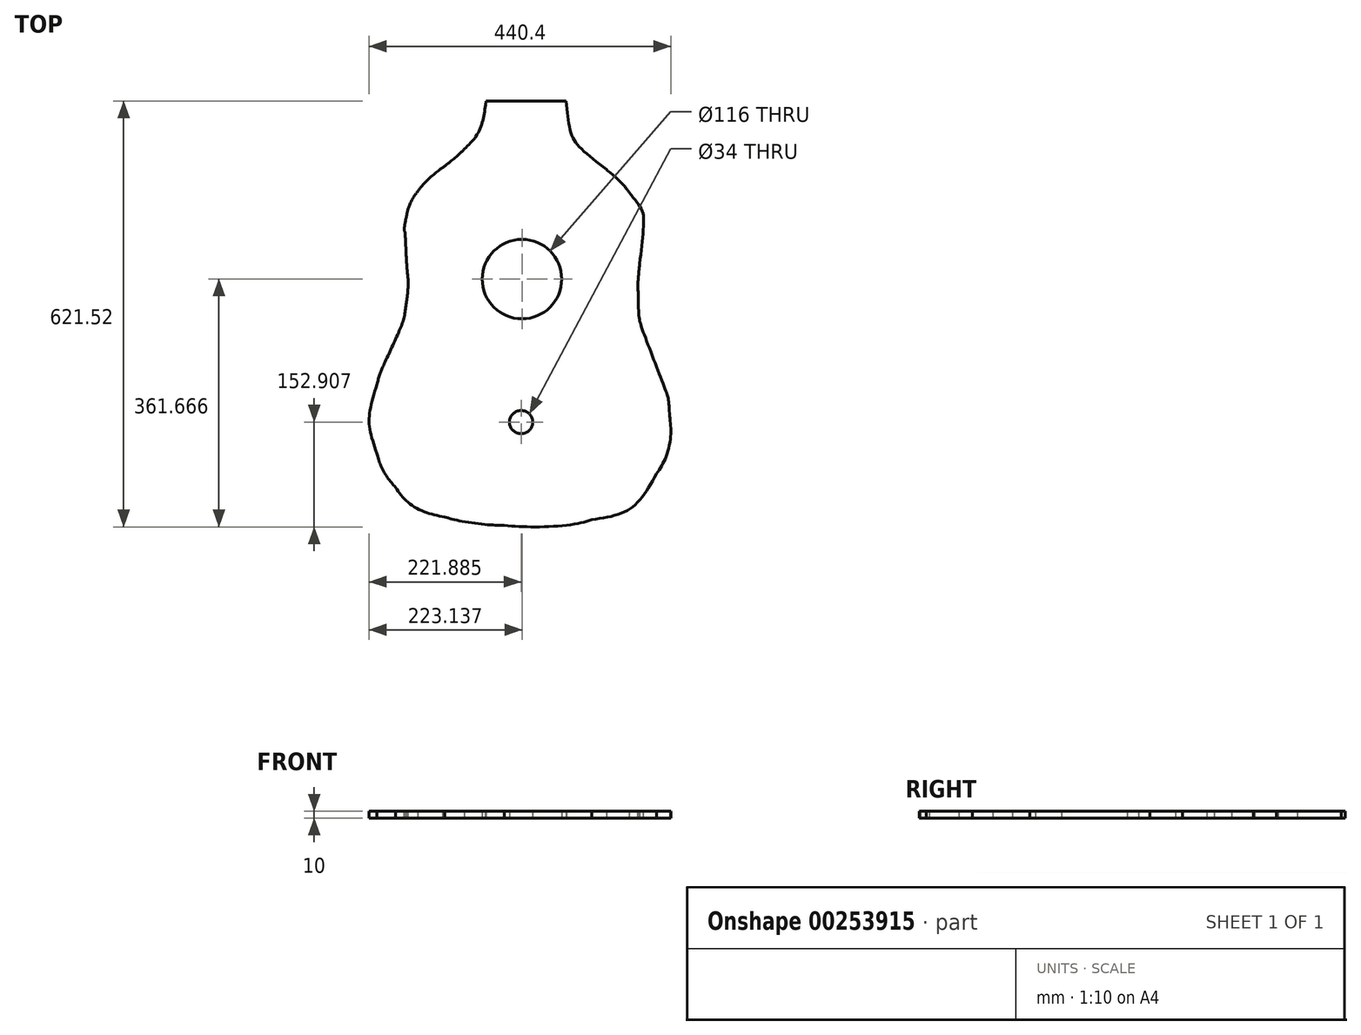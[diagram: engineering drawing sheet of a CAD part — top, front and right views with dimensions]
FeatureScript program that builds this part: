
annotation { "Feature Type Name" : "Feature", "Feature Type Description" : "" }
export const myFeature = defineFeature(function(context is Context, id is Id, definition is map)
    precondition{}
    {
        {
            var Q0;
            Q0=qCreatedBy(makeId("Top.planeOp"),FACE);
            var sketch = newSketch(context, id + "F0", { "sketchPlane" : qUnion([Q0])});
            skFitSpline(sketch, "E0", {"points": [v(-25.63, -554.96) * mm, v(-51.33, -553.75) * mm, v(-93.67, -547.73) * mm, v(-112.88, -542.55) * mm]});
            skFitSpline(sketch, "E1", {"points": [v(-112.88, -542.55) * mm, v(-142.24, -535.13) * mm, v(-168.61, -519.25) * mm, v(-184.46, -499.45) * mm]});
            skFitSpline(sketch, "E2", {"points": [v(-184.46, -499.45) * mm, v(-195.48, -486.1) * mm, v(-206.57, -466) * mm, v(-211.92, -449.7) * mm]});
            skFitSpline(sketch, "E3", {"points": [v(-211.92, -449.7) * mm, v(-221.91, -415.1) * mm, v(-221.87, -388.03) * mm, v(-211.77, -349.42) * mm]});
            skFitSpline(sketch, "E4", {"points": [v(-211.77, -349.42) * mm, v(-208.02, -335.83) * mm, v(-203.86, -325.36) * mm, v(-191.4, -298.17) * mm]});
            skFitSpline(sketch, "E5", {"points": [v(-191.4, -298.17) * mm, v(-179.07, -271.07) * mm, v(-172.16, -251.34) * mm, v(-169.81, -236.59) * mm]});
            skFitSpline(sketch, "E6", {"points": [v(-169.81, -236.59) * mm, v(-167.25, -220.4) * mm, v(-166.25, -197.26) * mm, v(-167.47, -182.89) * mm]});
            skFitSpline(sketch, "E7", {"points": [v(-167.47, -182.89) * mm, v(-168.08, -176.09) * mm, v(-169, -161.1) * mm, v(-169.51, -149.57) * mm]});
            skFitSpline(sketch, "E8", {"points": [v(-169.51, -149.57) * mm, v(-170.05, -138.04) * mm, v(-170.72, -127.61) * mm, v(-171, -126.4) * mm]});
            skFitSpline(sketch, "E9", {"points": [v(-171, -126.4) * mm, v(-171.65, -123.63) * mm, v(-170.05, -110.58) * mm, v(-167.88, -100.9) * mm]});
            skFitSpline(sketch, "E10", {"points": [v(-167.88, -100.9) * mm, v(-165.8, -91.55) * mm, v(-158.2, -75.69) * mm, v(-151.77, -67.21) * mm]});
            skFitSpline(sketch, "E11", {"points": [v(-151.77, -67.21) * mm, v(-145.48, -58.88) * mm, v(-127.22, -41.32) * mm, v(-116.1, -32.92) * mm]});
            skFitSpline(sketch, "E12", {"points": [v(-116.1, -32.92) * mm, v(-105.06, -24.56) * mm, v(-89.48, -11.2) * mm, v(-83.93, -5.31) * mm]});
            skFitSpline(sketch, "E13", {"points": [v(-83.93, -5.31) * mm, v(-68.52, 10.96) * mm, v(-57.93, 33.13) * mm, v(-53.21, 58.99) * mm]});
            skFitSpline(sketch, "E14", {"points": [v(-53.21, 58.99) * mm, v(-51.12, 70.34) * mm, v(-50.91, 75.7) * mm, v(-50.64, 125.07) * mm]});
            skFitSpline(sketch, "E15", {"points": [v(65.33, 58.7) * mm, v(71.3, 18.27) * mm, v(84.05, -2.46) * mm, v(123.21, -35.5) * mm]});
            skFitSpline(sketch, "E16", {"points": [v(123.21, -35.5) * mm, v(137.4, -47.48) * mm, v(149.94, -60.2) * mm, v(156.52, -69.26) * mm]});
            skFitSpline(sketch, "E17", {"points": [v(156.52, -69.26) * mm, v(174.53, -93.7) * mm, v(177.6, -114.5) * mm, v(171.85, -172.99) * mm]});
            skFitSpline(sketch, "E18", {"points": [v(171.85, -172.99) * mm, v(169.6, -196.17) * mm, v(169.26, -204.05) * mm, v(169.8, -220.64) * mm]});
            skFitSpline(sketch, "E19", {"points": [v(169.8, -220.64) * mm, v(170.9, -250.17) * mm, v(174.7, -265.7) * mm, v(192.33, -312.6) * mm]});
            skFitSpline(sketch, "E20", {"points": [v(192.33, -312.6) * mm, v(210.65, -360.23) * mm, v(213.58, -370.72) * mm, v(215.51, -395.3) * mm]});
            skFitSpline(sketch, "E21", {"points": [v(215.51, -395.3) * mm, v(217.15, -422.72) * mm, v(209.2, -457.39) * mm, v(196.22, -479.48) * mm]});
            skFitSpline(sketch, "E22", {"points": [v(196.22, -479.48) * mm, v(171.82, -518.02) * mm, v(144.73, -537.28) * mm, v(101.85, -546.55) * mm]});
            skFitSpline(sketch, "E23", {"points": [v(101.85, -546.55) * mm, v(75.69, -553.28) * mm, v(18.53, -557.04) * mm, v(-25.63, -554.96) * mm]});
            skCircle(sketch, "E24", {"center": v(0.06, -195.38) * mm, "radius": 58 * mm});
            skCircle(sketch, "E25", {"center": v(-1.2, -404.14) * mm, "radius": 17 * mm});
            skLineSegment(sketch, "E26", {"start": v(65.33, 58.7) * mm, "end": v(64.57, 64.47) * mm});
            skLineSegment(sketch, "E27", {"start": v(-52.3, 64.47) * mm, "end": v(64.57, 64.47) * mm});
            skLineSegment(sketch, "E28", {"start": v(-199.92, -555.53) * mm, "end": v(211.97, -555.53) * mm, "construction": true});
            skSolve(sketch);
        }
        {
            var Q0;
            Q0 = qSketchRegion(id + "F0", true);
            extrude(context, id + "F1", {"entities" : qUnion([Q0]), "depth" : 10 * mm});
        }
    });
